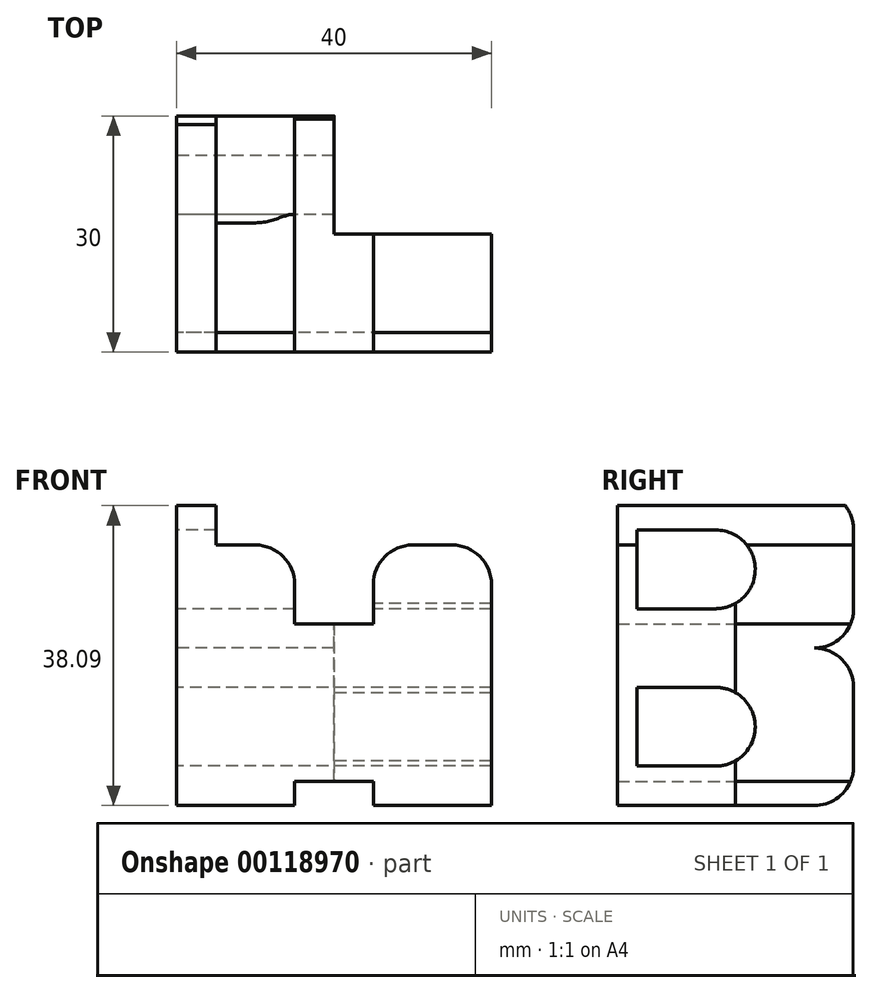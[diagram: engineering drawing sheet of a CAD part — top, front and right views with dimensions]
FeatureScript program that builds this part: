
annotation { "Feature Type Name" : "Feature", "Feature Type Description" : "" }
export const myFeature = defineFeature(function(context is Context, id is Id, definition is map)
    precondition{}
    {
        {
            var Q0;
            Q0=qCreatedBy(makeId("Top.planeOp"),FACE);
            var sketch = newSketch(context, id + "F0", { "sketchPlane" : qUnion([Q0])});
            skLineSegment(sketch, "E0.bottom", {"start": v(25, 25) * mm, "end": v(-25, 25) * mm, "construction": true});
            skLineSegment(sketch, "E0.top", {"start": v(25, -25) * mm, "end": v(-25, -25) * mm, "construction": true});
            skLineSegment(sketch, "E0.left", {"start": v(25, 25) * mm, "end": v(25, -25) * mm, "construction": true});
            skLineSegment(sketch, "E0.right", {"start": v(-25, 25) * mm, "end": v(-25, -25) * mm, "construction": true});
            skPoint(sketch, "E0.middle", {"position": v(0, 0) * mm});
            skLineSegment(sketch, "E1.bottom", {"start": v(20, 20) * mm, "end": v(-20, 20) * mm, "construction": true});
            skLineSegment(sketch, "E1.top", {"start": v(20, -20) * mm, "end": v(-20, -20) * mm, "construction": true});
            skLineSegment(sketch, "E1.left", {"start": v(20, 20) * mm, "end": v(20, -20) * mm, "construction": true});
            skLineSegment(sketch, "E1.right", {"start": v(-20, 20) * mm, "end": v(-20, -20) * mm, "construction": true});
            skLineSegment(sketch, "E2", {"start": v(-20, 20) * mm, "end": v(0, 20) * mm});
            skLineSegment(sketch, "E3", {"start": v(0, 20) * mm, "end": v(0, -5) * mm});
            skLineSegment(sketch, "E4", {"start": v(0, -5) * mm, "end": v(20, -5) * mm});
            skLineSegment(sketch, "E5", {"start": v(20, -5) * mm, "end": v(20, -20) * mm});
            skLineSegment(sketch, "E6", {"start": v(-20, -20) * mm, "end": v(-20, 20) * mm});
            skLineSegment(sketch, "E7", {"start": v(-20, -20) * mm, "end": v(20, -20) * mm});
            skSolve(sketch);
        }
        {
            var Q0;
            Q0=qCreatedBy(makeId("Right.planeOp"),FACE);
            var sketch = newSketch(context, id + "F1", { "sketchPlane" : qUnion([Q0])});
            skLineSegment(sketch, "E8.bottom", {"start": v(25, 25) * mm, "end": v(-25, 25) * mm, "construction": true});
            skLineSegment(sketch, "E8.top", {"start": v(25, -25) * mm, "end": v(-25, -25) * mm, "construction": true});
            skLineSegment(sketch, "E8.left", {"start": v(25, 25) * mm, "end": v(25, -25) * mm, "construction": true});
            skLineSegment(sketch, "E8.right", {"start": v(-25, 25) * mm, "end": v(-25, -25) * mm, "construction": true});
            skPoint(sketch, "E8.middle", {"position": v(0, 0) * mm});
            skLineSegment(sketch, "E9.bottom", {"start": v(5, 20) * mm, "end": v(-20, 20) * mm, "construction": true});
            skLineSegment(sketch, "E9.top", {"start": v(5, -20) * mm, "end": v(-20, -20) * mm, "construction": true});
            skLineSegment(sketch, "E9.left", {"start": v(20, 20) * mm, "end": v(20, -20) * mm, "construction": true});
            skLineSegment(sketch, "E9.right", {"start": v(-20, 20) * mm, "end": v(-20, -20) * mm, "construction": true});
            skLineSegment(sketch, "E10", {"start": v(-20, 20) * mm, "end": v(-20, -20) * mm});
            skLineSegment(sketch, "E11", {"start": v(-20, -20) * mm, "end": v(5, -20) * mm});
            skLineSegment(sketch, "E12", {"start": v(-20, 20) * mm, "end": v(5, 20) * mm});
            skPoint(sketch, "E13.center.orphan", {"position": v(-10, 10) * mm});
            skPoint(sketch, "E14.center.orphan", {"position": v(-10, -10) * mm});
            skLineSegment(sketch, "E15.bottom", {"start": v(-7.5, 15) * mm, "end": v(-17.5, 15) * mm});
            skLineSegment(sketch, "E15.top", {"start": v(-7.5, 5) * mm, "end": v(-17.5, 5) * mm});
            skLineSegment(sketch, "E15.left", {"start": v(-2.5, 10) * mm, "end": v(-2.5, 10) * mm});
            skLineSegment(sketch, "E15.right", {"start": v(-17.5, 15) * mm, "end": v(-17.5, 5) * mm});
            skPoint(sketch, "E16.visualSharp", {"position": v(-2.5, 15) * mm});
            skArc(sketch, "E16.filletArc", {"start": v(-2.5, 10) * mm, "mid": v(-3.96, 13.54) * mm, "end": v(-7.5, 15) * mm});
            skPoint(sketch, "E17.visualSharp", {"position": v(-2.5, 5) * mm});
            skArc(sketch, "E17.filletArc", {"start": v(-7.5, 5) * mm, "mid": v(-3.96, 6.46) * mm, "end": v(-2.5, 10) * mm});
            skLineSegment(sketch, "E18.bottom", {"start": v(-7.5, -5) * mm, "end": v(-17.5, -5) * mm});
            skLineSegment(sketch, "E18.top", {"start": v(-7.5, -15) * mm, "end": v(-17.5, -15) * mm});
            skLineSegment(sketch, "E18.left", {"start": v(-2.5, -10) * mm, "end": v(-2.5, -10) * mm});
            skLineSegment(sketch, "E18.right", {"start": v(-17.5, -5) * mm, "end": v(-17.5, -15) * mm});
            skPoint(sketch, "E19.visualSharp", {"position": v(-2.5, -5) * mm});
            skArc(sketch, "E19.filletArc", {"start": v(-2.5, -10) * mm, "mid": v(-3.96, -6.46) * mm, "end": v(-7.5, -5) * mm});
            skPoint(sketch, "E20.visualSharp", {"position": v(-2.5, -15) * mm});
            skArc(sketch, "E20.filletArc", {"start": v(-7.5, -15) * mm, "mid": v(-3.96, -13.54) * mm, "end": v(-2.5, -10) * mm});
            skLineSegment(sketch, "E21", {"start": v(10, -15) * mm, "end": v(10, -5) * mm});
            skPoint(sketch, "E22.newPointB", {"position": v(20, -20) * mm});
            skArc(sketch, "E22.filletArc", {"start": v(5, -20) * mm, "mid": v(8.54, -18.54) * mm, "end": v(10, -15) * mm});
            skPoint(sketch, "E23.visualSharp", {"position": v(10, 0) * mm});
            skArc(sketch, "E23.filletArc", {"start": v(10, -5) * mm, "mid": v(8.54, -1.46) * mm, "end": v(5, 0) * mm});
            skLineSegment(sketch, "E24", {"start": v(10, 5) * mm, "end": v(10, 15) * mm});
            skArc(sketch, "E25.filletArc", {"start": v(5, 0) * mm, "mid": v(8.54, 1.46) * mm, "end": v(10, 5) * mm});
            skPoint(sketch, "E26.newPointA", {"position": v(20, 20) * mm});
            skArc(sketch, "E26.filletArc", {"start": v(10, 15) * mm, "mid": v(8.54, 18.54) * mm, "end": v(5, 20) * mm});
            skPoint(sketch, "E27.visualSharp", {"position": v(5, 20) * mm});
            skLineSegment(sketch, "E27.filletArc", {"start": v(5, 20) * mm, "end": v(5, 20) * mm});
            skPoint(sketch, "E28.visualSharp", {"position": v(10, 5) * mm});
            skLineSegment(sketch, "E28.filletArc", {"start": v(10, 5) * mm, "end": v(10, 5) * mm});
            skSolve(sketch);
        }
        {
            var Q0;
            Q0=qCreatedBy(makeId("Front.planeOp"),FACE);
            var sketch = newSketch(context, id + "F2", { "sketchPlane" : qUnion([Q0])});
            skLineSegment(sketch, "E29.bottom", {"start": v(25, 25) * mm, "end": v(-25, 25) * mm, "construction": true});
            skLineSegment(sketch, "E29.top", {"start": v(25, -25) * mm, "end": v(-25, -25) * mm, "construction": true});
            skLineSegment(sketch, "E29.left", {"start": v(25, 25) * mm, "end": v(25, -25) * mm, "construction": true});
            skLineSegment(sketch, "E29.right", {"start": v(-25, 25) * mm, "end": v(-25, -25) * mm, "construction": true});
            skPoint(sketch, "E29.middle", {"position": v(0, 0) * mm});
            skLineSegment(sketch, "E30.bottom", {"start": v(20, 18.1) * mm, "end": v(-20, 18.1) * mm, "construction": true});
            skLineSegment(sketch, "E30.top", {"start": v(20, -21.9) * mm, "end": v(-20, -21.9) * mm, "construction": true});
            skLineSegment(sketch, "E30.left", {"start": v(20, 8.1) * mm, "end": v(20, -21.9) * mm, "construction": true});
            skLineSegment(sketch, "E30.right", {"start": v(-20, 18.1) * mm, "end": v(-20, -21.9) * mm, "construction": true});
            skPoint(sketch, "E30.middle", {"position": v(0, -1.9) * mm});
            skLineSegment(sketch, "E31.bottom", {"start": v(-20, 18.1) * mm, "end": v(-15, 18.1) * mm});
            skLineSegment(sketch, "E31.top", {"start": v(-20, 13.1) * mm, "end": v(-15, 13.1) * mm});
            skLineSegment(sketch, "E31.left", {"start": v(-20, 18.1) * mm, "end": v(-20, 13.1) * mm});
            skLineSegment(sketch, "E31.right", {"start": v(-15, 18.1) * mm, "end": v(-15, 13.1) * mm});
            skLineSegment(sketch, "E32.bottom", {"start": v(-20, 13.1) * mm, "end": v(-10, 13.1) * mm});
            skLineSegment(sketch, "E32.top", {"start": v(-20, -21.9) * mm, "end": v(-5, -21.9) * mm});
            skLineSegment(sketch, "E32.left", {"start": v(-20, 13.1) * mm, "end": v(-20, -21.9) * mm});
            skLineSegment(sketch, "E32.right", {"start": v(-5, 8.1) * mm, "end": v(-5, -21.9) * mm});
            skLineSegment(sketch, "E33.bottom", {"start": v(-5, 3.1) * mm, "end": v(5, 3.1) * mm});
            skLineSegment(sketch, "E33.top", {"start": v(-5, -16.9) * mm, "end": v(5, -16.9) * mm});
            skLineSegment(sketch, "E33.left", {"start": v(-5, 3.1) * mm, "end": v(-5, -16.9) * mm});
            skLineSegment(sketch, "E33.right", {"start": v(5, 3.1) * mm, "end": v(5, -16.9) * mm});
            skLineSegment(sketch, "E34.bottom", {"start": v(10, 13.1) * mm, "end": v(15, 13.1) * mm});
            skLineSegment(sketch, "E34.top", {"start": v(5, -21.9) * mm, "end": v(20, -21.9) * mm});
            skLineSegment(sketch, "E34.left", {"start": v(5, 8.1) * mm, "end": v(5, -21.9) * mm});
            skLineSegment(sketch, "E34.right", {"start": v(20, 8.1) * mm, "end": v(20, -21.9) * mm});
            skPoint(sketch, "E35.visualSharp", {"position": v(-5, 13.1) * mm});
            skArc(sketch, "E35.filletArc", {"start": v(-5, 8.1) * mm, "mid": v(-6.46, 11.63) * mm, "end": v(-10, 13.1) * mm});
            skPoint(sketch, "E36.visualSharp", {"position": v(5, 13.1) * mm});
            skArc(sketch, "E36.filletArc", {"start": v(10, 13.1) * mm, "mid": v(6.46, 11.63) * mm, "end": v(5, 8.1) * mm});
            skPoint(sketch, "E37.newPointB", {"position": v(20, 18.1) * mm});
            skArc(sketch, "E37.filletArc", {"start": v(20, 8.1) * mm, "mid": v(18.54, 11.63) * mm, "end": v(15, 13.1) * mm});
            skSolve(sketch);
        }
        {
            var Q0;
            Q0 = qSketchRegion(id + "F0", true);
            extrude(context, id + "F3", {"entities" : qUnion([Q0]), "endBound" : BoundingType.SYMMETRIC, "depth" : 50 * mm});
        }
        {
            var Q0;
            Q0 = qSketchRegion(id + "F1", true);
            extrude(context, id + "F4", {"entities" : qUnion([Q0]), "operationType" : NewBodyOperationType.INTERSECT, "endBound" : BoundingType.SYMMETRIC, "depth" : 50 * mm});
        }
        {
            var Q0;
            Q0 = qSketchRegion(id + "F2", true);
            extrude(context, id + "F5", {"entities" : qUnion([Q0]), "operationType" : NewBodyOperationType.INTERSECT, "endBound" : BoundingType.SYMMETRIC, "depth" : 50 * mm});
        }
    });
